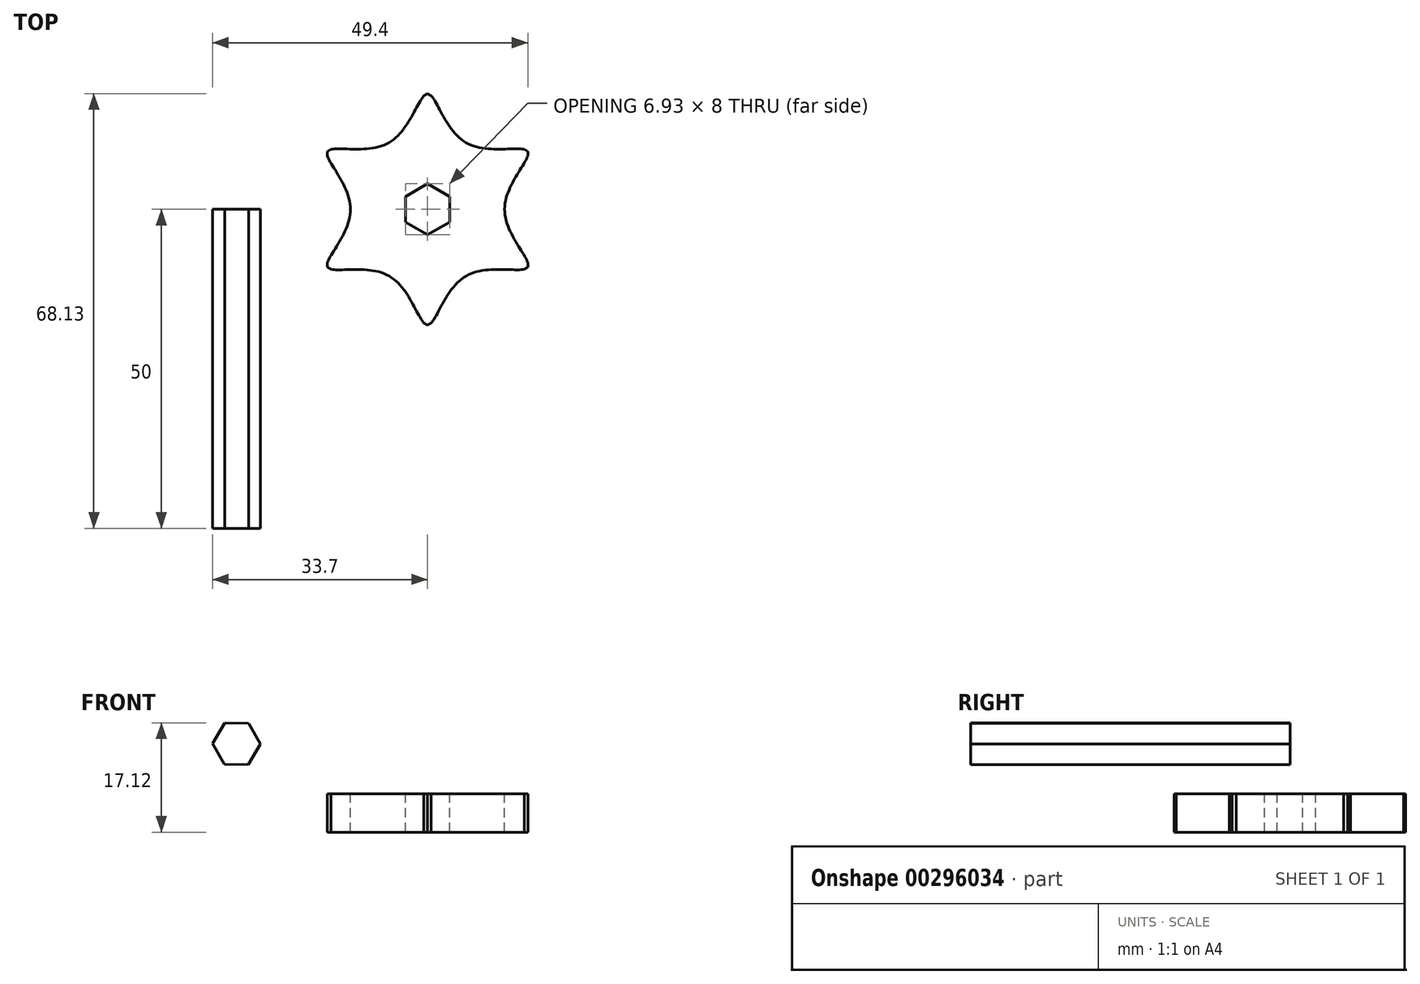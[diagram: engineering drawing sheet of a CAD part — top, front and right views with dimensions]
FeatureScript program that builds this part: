
annotation { "Feature Type Name" : "Feature", "Feature Type Description" : "" }
export const myFeature = defineFeature(function(context is Context, id is Id, definition is map)
    precondition{}
    {
        {
            var Q0;
            Q0=qCreatedBy(makeId("Front.planeOp"),FACE);
            var sketch = newSketch(context, id + "F0", { "sketchPlane" : qUnion([Q0])});
            skCircle(sketch, "E0.cCircle", {"center": v(-29.95, 13.85) * mm, "radius": 3.25 * mm, "construction": true});
            skLineSegment(sketch, "E0.0", {"start": v(-28.04, 17.08) * mm, "end": v(-26.2, 13.81) * mm});
            skLineSegment(sketch, "E0.1", {"start": v(-26.2, 13.81) * mm, "end": v(-28.12, 10.59) * mm});
            skLineSegment(sketch, "E0.2", {"start": v(-28.12, 10.59) * mm, "end": v(-31.87, 10.63) * mm});
            skLineSegment(sketch, "E0.3", {"start": v(-31.87, 10.63) * mm, "end": v(-33.7, 13.9) * mm});
            skLineSegment(sketch, "E0.4", {"start": v(-33.7, 13.9) * mm, "end": v(-31.8, 17.12) * mm});
            skLineSegment(sketch, "E0.5", {"start": v(-31.8, 17.12) * mm, "end": v(-28.04, 17.08) * mm});
            skPoint(sketch, "E0.0.midPoint", {"position": v(-27.12, 15.45) * mm});
            skSolve(sketch);
        }
        {
            var Q0;
            Q0=makeQuery(id+"F0.imprint","IMPRINT",FACE,{"disambiguationData":[TD([[makeQuery(id+"F0.imprint","IMPRINT",EDGE,{"derivedFrom":sQuery(id+"F0.wireOp",EDGE,"E0.0")}),-1.0]])]});
            extrude(context, id + "F1", {"entities" : qUnion([Q0]), "depth" : 50 * mm});
        }
        {
            var Q0;
            Q0=qCreatedBy(makeId("Top.planeOp"),FACE);
            var sketch = newSketch(context, id + "F2", { "sketchPlane" : qUnion([Q0])});
            skCircle(sketch, "E1.cCircle", {"center": v(0, 0) * mm, "radius": 15.7 * mm, "construction": true});
            skLineSegment(sketch, "E1.0", {"start": v(15.7, 9.07) * mm, "end": v(15.7, -9.07) * mm});
            skLineSegment(sketch, "E1.1", {"start": v(15.7, -9.07) * mm, "end": v(0, -18.13) * mm});
            skLineSegment(sketch, "E1.2", {"start": v(0, -18.13) * mm, "end": v(-15.7, -9.07) * mm});
            skLineSegment(sketch, "E1.3", {"start": v(-15.7, -9.07) * mm, "end": v(-15.7, 9.07) * mm});
            skLineSegment(sketch, "E1.4", {"start": v(-15.7, 9.07) * mm, "end": v(0, 18.13) * mm});
            skLineSegment(sketch, "E1.5", {"start": v(0, 18.13) * mm, "end": v(15.7, 9.07) * mm});
            skPoint(sketch, "E1.0.midPoint", {"position": v(15.7, 0) * mm});
            skCircle(sketch, "E2.cCircle", {"center": v(0, 0) * mm, "radius": 10.45 * mm, "construction": true});
            skLineSegment(sketch, "E2.0", {"start": v(6.02, 10.45) * mm, "end": v(12.06, 0.01) * mm});
            skLineSegment(sketch, "E2.1", {"start": v(12.06, 0.01) * mm, "end": v(6.04, -10.44) * mm});
            skLineSegment(sketch, "E2.2", {"start": v(6.04, -10.44) * mm, "end": v(-6.02, -10.45) * mm});
            skLineSegment(sketch, "E2.3", {"start": v(-6.02, -10.45) * mm, "end": v(-12.06, -0.01) * mm});
            skLineSegment(sketch, "E2.4", {"start": v(-12.06, -0.01) * mm, "end": v(-6.04, 10.44) * mm});
            skLineSegment(sketch, "E2.5", {"start": v(-6.04, 10.44) * mm, "end": v(6.02, 10.45) * mm});
            skPoint(sketch, "E2.0.midPoint", {"position": v(9.04, 5.23) * mm});
            skFitSpline(sketch, "E3", {"points": [v(-15.7, 9.07) * mm, v(-6.04, 10.44) * mm, v(0, 18.13) * mm, v(6.02, 10.45) * mm, v(15.7, 9.07) * mm, v(12.06, 0.01) * mm, v(15.7, -9.07) * mm, v(6.04, -10.44) * mm, v(0, -18.13) * mm, v(-6.02, -10.45) * mm, v(-15.7, -9.07) * mm, v(-12.06, -0.01) * mm, v(-15.7, 9.07) * mm]});
            skSolve(sketch);
        }
        {
            var Q0;
            {var subQ1=sQuery(id+"F2.wireOp",EDGE,"E2.4");Q0=makeQuery(id+"F2.imprint","IMPRINT",FACE,{"disambiguationData":[TD([[makeQuery(id+"F2.imprint","IMPRINT",EDGE,{"derivedFrom":subQ1}),1.0]])]});}
            var Q1;
            Q1=makeQuery(id+"F2.imprint","IMPRINT",FACE,{"disambiguationData":[TD([[makeQuery(id+"F2.imprint","IMPRINT",EDGE,{"derivedFrom":sQuery(id+"F2.wireOp",EDGE,"E2.0")}),-1.0]])]});
            var Q2;
            {var subQ1=sQuery(id+"F2.wireOp",EDGE,"E2.5");Q2=makeQuery(id+"F2.imprint","IMPRINT",FACE,{"disambiguationData":[TD([[makeQuery(id+"F2.imprint","IMPRINT",EDGE,{"derivedFrom":subQ1}),1.0]])]});}
            var Q3;
            {var subQ0=sQuery(id+"F2.wireOp",EDGE,"E2.0");Q3=makeQuery(id+"F2.imprint","IMPRINT",FACE,{"disambiguationData":[TD([[makeQuery(id+"F2.imprint","IMPRINT",EDGE,{"derivedFrom":subQ0}),1.0]])]});}
            var Q4;
            {var subQ1=sQuery(id+"F2.wireOp",EDGE,"E2.1");Q4=makeQuery(id+"F2.imprint","IMPRINT",FACE,{"disambiguationData":[TD([[makeQuery(id+"F2.imprint","IMPRINT",EDGE,{"derivedFrom":subQ1}),1.0]])]});}
            var Q5;
            {var subQ1=sQuery(id+"F2.wireOp",EDGE,"E2.2");Q5=makeQuery(id+"F2.imprint","IMPRINT",FACE,{"disambiguationData":[TD([[makeQuery(id+"F2.imprint","IMPRINT",EDGE,{"derivedFrom":subQ1}),1.0]])]});}
            var Q6;
            {var subQ1=sQuery(id+"F2.wireOp",EDGE,"E2.3");Q6=makeQuery(id+"F2.imprint","IMPRINT",FACE,{"disambiguationData":[TD([[makeQuery(id+"F2.imprint","IMPRINT",EDGE,{"derivedFrom":subQ1}),1.0]])]});}
            var Q7;
            Q7=sQuery(id+"F2.wireOp",EDGE,"E3");
            extrude(context, id + "F3", {"entities" : qUnion([Q0, Q1, Q2, Q3, Q4, Q5, Q6]), "surfaceEntities" : qUnion([Q7]), "depth" : 6 * mm});
        }
        {
            var Q0;
            Q0=makeQuery(id+"F3.opExtrude","CAP_FACE",FACE,{"disambiguationData":[OSD([sQuery(id+"F2.wireOp",EDGE,"E1.0"),sQuery(id+"F2.wireOp",EDGE,"E1.1"),sQuery(id+"F2.wireOp",EDGE,"E1.2"),sQuery(id+"F2.wireOp",EDGE,"E1.3"),sQuery(id+"F2.wireOp",EDGE,"E1.4"),sQuery(id+"F2.wireOp",EDGE,"E1.5"),sQuery(id+"F2.wireOp",EDGE,"E3")])],"isStart":false});
            var sketch = newSketch(context, id + "F4", { "sketchPlane" : qUnion([Q0])});
            skCircle(sketch, "E4.cCircle", {"center": v(0, 0) * mm, "radius": 3.46 * mm, "construction": true});
            skLineSegment(sketch, "E4.0", {"start": v(3.46, 2) * mm, "end": v(3.46, -2) * mm});
            skLineSegment(sketch, "E4.1", {"start": v(3.46, -2) * mm, "end": v(0, -4) * mm});
            skLineSegment(sketch, "E4.2", {"start": v(0, -4) * mm, "end": v(-3.46, -2) * mm});
            skLineSegment(sketch, "E4.3", {"start": v(-3.46, -2) * mm, "end": v(-3.46, 2) * mm});
            skLineSegment(sketch, "E4.4", {"start": v(-3.46, 2) * mm, "end": v(0, 4) * mm});
            skLineSegment(sketch, "E4.5", {"start": v(0, 4) * mm, "end": v(3.46, 2) * mm});
            skPoint(sketch, "E4.0.midPoint", {"position": v(3.46, 0) * mm});
            skSolve(sketch);
        }
        {
            var Q0;
            Q0=makeQuery(id+"F4.imprint","IMPRINT",FACE,{"disambiguationData":[TD([[makeQuery(id+"F4.imprint","IMPRINT",EDGE,{"derivedFrom":sQuery(id+"F4.wireOp",EDGE,"E4.0")}),-1.0]])]});
            extrude(context, id + "F5", {"entities" : qUnion([Q0]), "operationType" : NewBodyOperationType.REMOVE, "oppositeDirection" : true, "depth" : 25 * mm});
        }
    });
